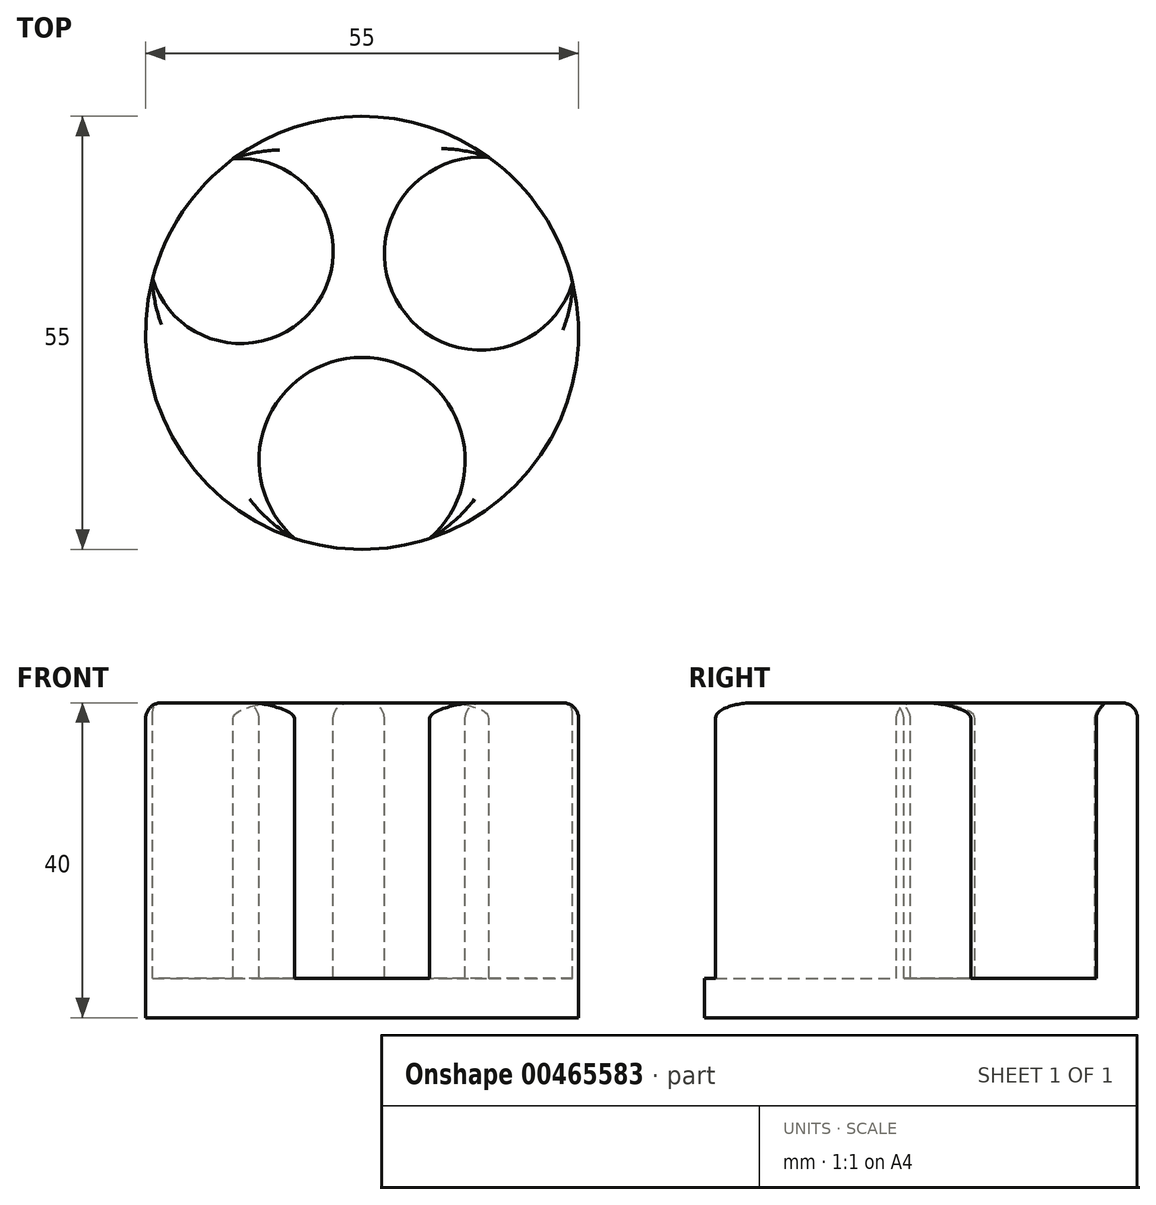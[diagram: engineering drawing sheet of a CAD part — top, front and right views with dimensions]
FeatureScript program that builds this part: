
annotation { "Feature Type Name" : "Feature", "Feature Type Description" : "" }
export const myFeature = defineFeature(function(context is Context, id is Id, definition is map)
    precondition{}
    {
        {
            var Q0;
            Q0=qCreatedBy(makeId("Top.planeOp"),FACE);
            var sketch = newSketch(context, id + "F0", { "sketchPlane" : qUnion([Q0])});
            skCircle(sketch, "E0", {"center": v(0, 0) * mm, "radius": 27.5 * mm});
            skSolve(sketch);
        }
        {
            var Q0;
            Q0 = qSketchRegion(id + "F0", true);
            extrude(context, id + "F1", {"entities" : qUnion([Q0]), "depth" : 40 * mm, "offsetDistance" : 25 * mm});
        }
        {
            var Q0;
            Q0=makeQuery(id+"F1.opExtrude","CAP_FACE",FACE,{"disambiguationData":[OSD([sQuery(id+"F0.wireOp",EDGE,"E0")])],"isStart":true});
            cPlane(context, id + "F2", {"entities" : qUnion([Q0]), "cplaneType" : CPlaneType.OFFSET, "offset" : 5 * mm, "oppositeDirection" : true, "width" : 150 * mm, "height" : 150 * mm});
        }
        {
            var Q0;
            Q0=makeQuery(id+"F1.opExtrude","CAP_FACE",FACE,{"disambiguationData":[OSD([sQuery(id+"F0.wireOp",EDGE,"E0")])],"isStart":false});
            var sketch = newSketch(context, id + "F3", { "sketchPlane" : qUnion([Q0])});
            skCircle(sketch, "E1", {"center": v(-15.42, 10.4) * mm, "radius": 11.75 * mm});
            skCircle(sketch, "E2", {"center": v(15.08, 10.05) * mm, "radius": 12.25 * mm});
            skCircle(sketch, "E3", {"center": v(0, -16.23) * mm, "radius": 13.1 * mm});
            skSolve(sketch);
        }
        {
            var Q0;
            Q0 = qSketchRegion(id + "F3", true);
            var Q1;
            Q1=qCreatedBy(id+"F2.planeOp",FACE);
            extrude(context, id + "F4", {"entities" : qUnion([Q0]), "operationType" : NewBodyOperationType.REMOVE, "endBound" : BoundingType.UP_TO_SURFACE, "oppositeDirection" : true, "endBoundEntityFace" : qUnion([Q1]), "depth" : 95 * mm, "offsetDistance" : 25 * mm});
        }
        {
            var Q0;
            Q0=makeQuery(id+"F1.opExtrude","CAP_FACE",FACE,{"disambiguationData":[OSD([sQuery(id+"F0.wireOp",EDGE,"E0")])],"isStart":false});
            fillet(context, id + "F5", {"entities" : qUnion([Q0]), "radius" : 2 * mm, "tangentPropagation" : true, "allowEdgeOverflow" : false});
        }
    });
